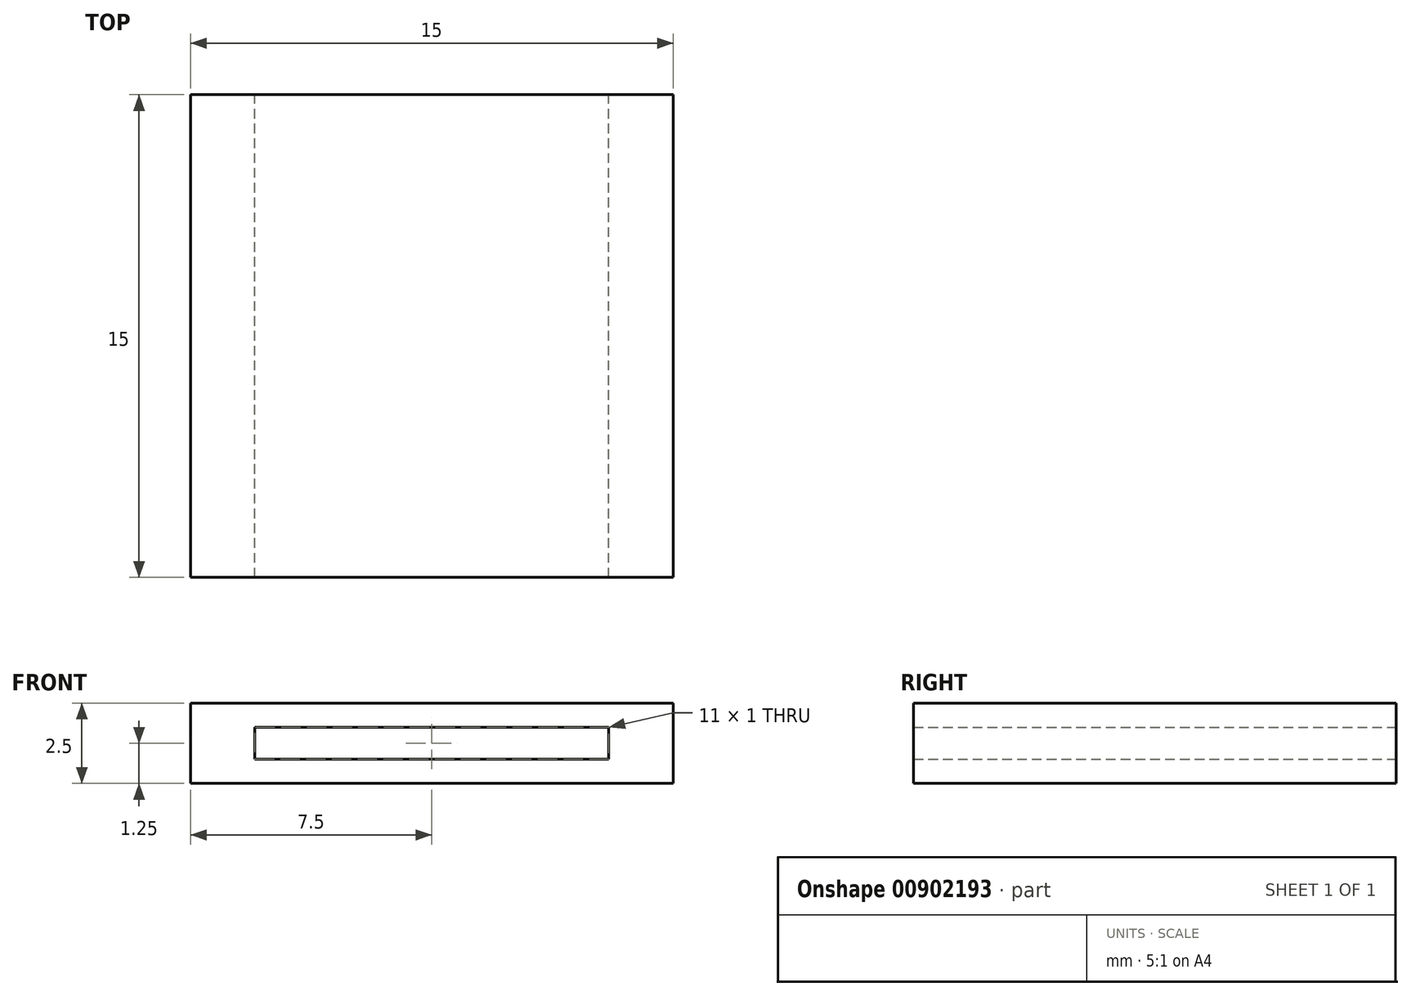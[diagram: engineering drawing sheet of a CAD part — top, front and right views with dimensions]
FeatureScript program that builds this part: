
annotation { "Feature Type Name" : "Feature", "Feature Type Description" : "" }
export const myFeature = defineFeature(function(context is Context, id is Id, definition is map)
    precondition{}
    {
        {
            var Q0;
            Q0=qCreatedBy(makeId("Front.planeOp"),FACE);
            var sketch = newSketch(context, id + "F0", { "sketchPlane" : qUnion([Q0])});
            skLineSegment(sketch, "E0.bottom", {"start": v(0, 0) * mm, "end": v(15, 0) * mm});
            skLineSegment(sketch, "E0.top", {"start": v(0, 2.5) * mm, "end": v(15, 2.5) * mm});
            skLineSegment(sketch, "E0.left", {"start": v(0, 0) * mm, "end": v(0, 2.5) * mm});
            skLineSegment(sketch, "E0.right", {"start": v(15, 0) * mm, "end": v(15, 2.5) * mm});
            skLineSegment(sketch, "E1.bottom", {"start": v(2, 1.75) * mm, "end": v(13, 1.75) * mm});
            skLineSegment(sketch, "E1.top", {"start": v(2, 0.75) * mm, "end": v(13, 0.75) * mm});
            skLineSegment(sketch, "E1.left", {"start": v(2, 1.75) * mm, "end": v(2, 0.75) * mm});
            skLineSegment(sketch, "E1.right", {"start": v(13, 1.75) * mm, "end": v(13, 0.75) * mm});
            skSolve(sketch);
        }
        {
            var Q0;
            Q0=qSketchRegion(id+"F0",true);
            extrude(context, id + "F1", {"entities" : qUnion([Q0]), "depth" : 15 * mm, "offsetDistance" : 25 * mm});
        }
    });
